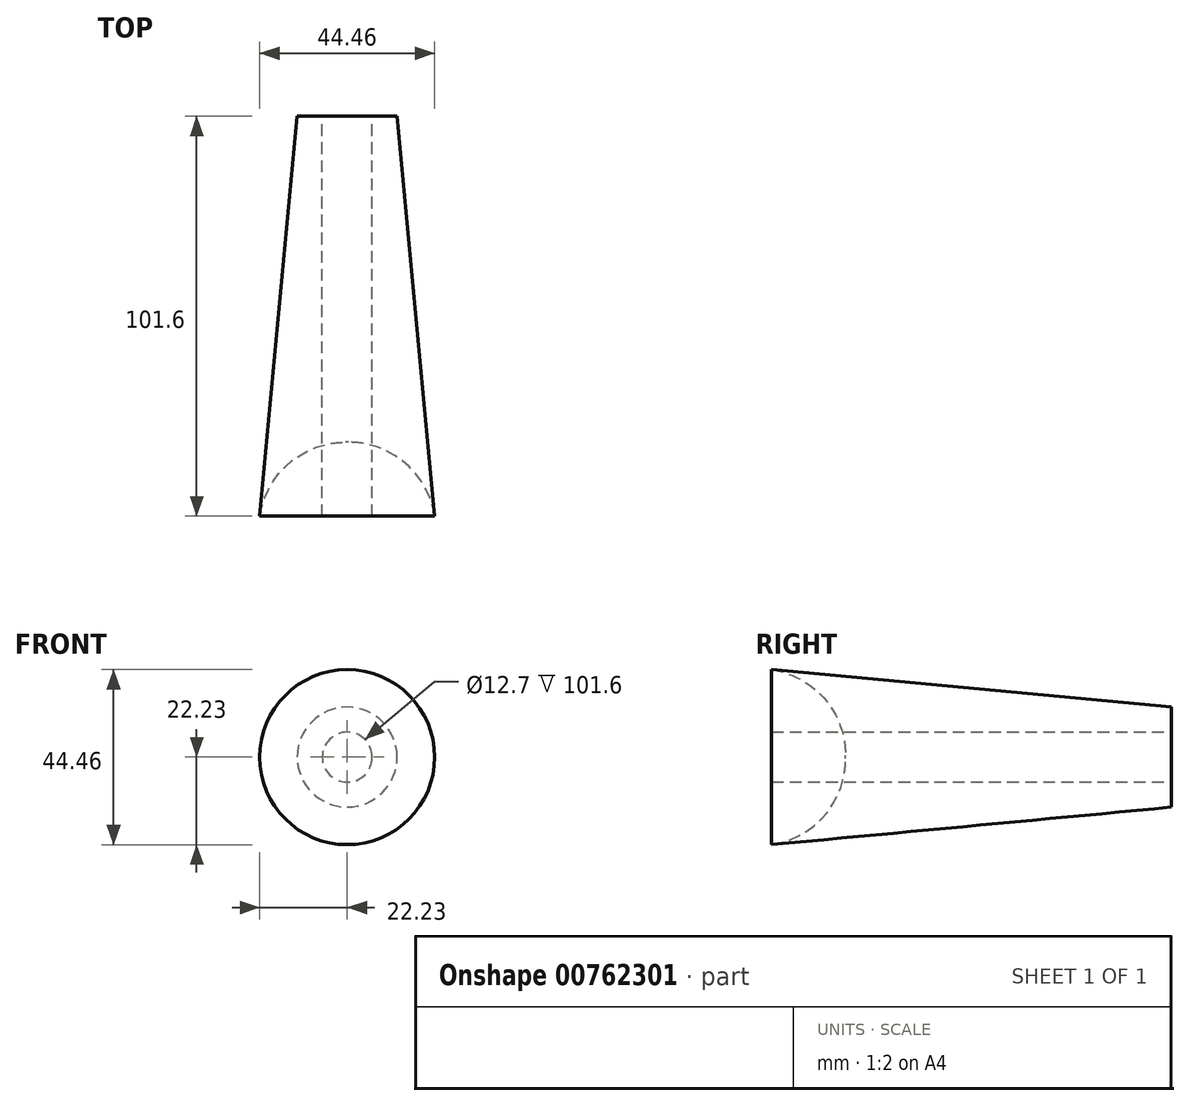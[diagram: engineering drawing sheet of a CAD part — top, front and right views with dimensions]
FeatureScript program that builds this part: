
annotation { "Feature Type Name" : "Feature", "Feature Type Description" : "" }
export const myFeature = defineFeature(function(context is Context, id is Id, definition is map)
    precondition{}
    {
        {
            var Q0;
            Q0=qCreatedBy(makeId("Front.planeOp"),FACE);
            var sketch = newSketch(context, id + "F0", { "sketchPlane" : qUnion([Q0])});
            skCircle(sketch, "E0", {"center": v(0, 0) * mm, "radius": 12.7 * mm});
            skSolve(sketch);
        }
        {
            var Q0;
            Q0=qCreatedBy(makeId("Front.planeOp"),FACE);
            cPlane(context, id + "F1", {"entities" : qUnion([Q0]), "cplaneType" : CPlaneType.OFFSET, "offset" : 101.6 * mm, "width" : 152.4 * mm, "height" : 152.4 * mm});
        }
        {
            var Q0;
            Q0=qCreatedBy(id+"F1.planeOp",FACE);
            var sketch = newSketch(context, id + "F2", { "sketchPlane" : qUnion([Q0])});
            skCircle(sketch, "E1", {"center": v(0, 0) * mm, "radius": 22.23 * mm});
            skSolve(sketch);
        }
        {
            var Q0;
            Q0=makeQuery(id+"F0.imprint","IMPRINT",FACE,{"disambiguationData":[TD([[makeQuery(id+"F0.imprint","IMPRINT",EDGE,{"derivedFrom":sQuery(id+"F0.wireOp",EDGE,"E0")}),1.0]])]});
            var Q1;
            Q1=makeQuery(id+"F2.imprint","IMPRINT",FACE,{"disambiguationData":[TD([[makeQuery(id+"F2.imprint","IMPRINT",EDGE,{"derivedFrom":sQuery(id+"F2.wireOp",EDGE,"E1")}),1.0]])]});
            loft(context, id + "F3", {"sheetProfilesArray" : [{ "sheetProfileEntities" : qUnion([Q0]) }, { "sheetProfileEntities" : qUnion([Q1]) }]});
        }
        {
            var Q0;
            Q0=qCreatedBy(makeId("Right.planeOp"),FACE);
            var sketch = newSketch(context, id + "F4", { "sketchPlane" : qUnion([Q0])});
            skLineSegment(sketch, "E2", {"start": v(-101.6, 0) * mm, "end": v(-127, 0) * mm});
            skLineSegment(sketch, "E3", {"start": v(-101.6, 0) * mm, "end": v(-101.6, 22.22) * mm});
            skArc(sketch, "E4", {"start": v(-101.6, 22.22) * mm, "mid": v(-119.46, 17) * mm, "end": v(-127, 0) * mm});
            skSolve(sketch);
        }
        {
            var Q0;
            Q0=makeQuery(id+"F4.imprint","IMPRINT",FACE,{"disambiguationData":[TD([[makeQuery(id+"F4.imprint","IMPRINT",EDGE,{"derivedFrom":sQuery(id+"F4.wireOp",EDGE,"E2")}),-1.0]])]});
            var Q1;
            Q1=sQuery(id+"F4.wireOp",EDGE,"E2");
            revolve(context, id + "F5", {"operationType" : NewBodyOperationType.ADD, "surfaceOperationType" : NewSurfaceOperationType.NEW, "entities" : qUnion([Q0]), "axis" : qUnion([Q1]), "revolveType" : RevolveType.FULL});
        }
        {
            var Q0;
            Q0=makeQuery(id+"F3.opLoft","CAP_FACE",FACE,{"disambiguationData":[OSD([makeQuery(id+"F0.imprint","IMPRINT",FACE,{"disambiguationData":[TD([[makeQuery(id+"F0.imprint","IMPRINT",EDGE,{"derivedFrom":sQuery(id+"F0.wireOp",EDGE,"E0")}),1.0]])]})])],"isStart":true});
            var sketch = newSketch(context, id + "F6", { "sketchPlane" : qUnion([Q0])});
            skCircle(sketch, "E5", {"center": v(0, 0) * mm, "radius": 6.35 * mm});
            skSolve(sketch);
        }
        {
            var Q0;
            Q0=makeQuery(id+"F6.imprint","IMPRINT",FACE,{"disambiguationData":[TD([[makeQuery(id+"F6.imprint","IMPRINT",EDGE,{"derivedFrom":sQuery(id+"F6.wireOp",EDGE,"E5")}),1.0]])]});
            extrude(context, id + "F7", {"entities" : qUnion([Q0]), "operationType" : NewBodyOperationType.REMOVE, "oppositeDirection" : true, "depth" : 101.6 * mm, "offsetDistance" : 25.4 * mm});
        }
    });
